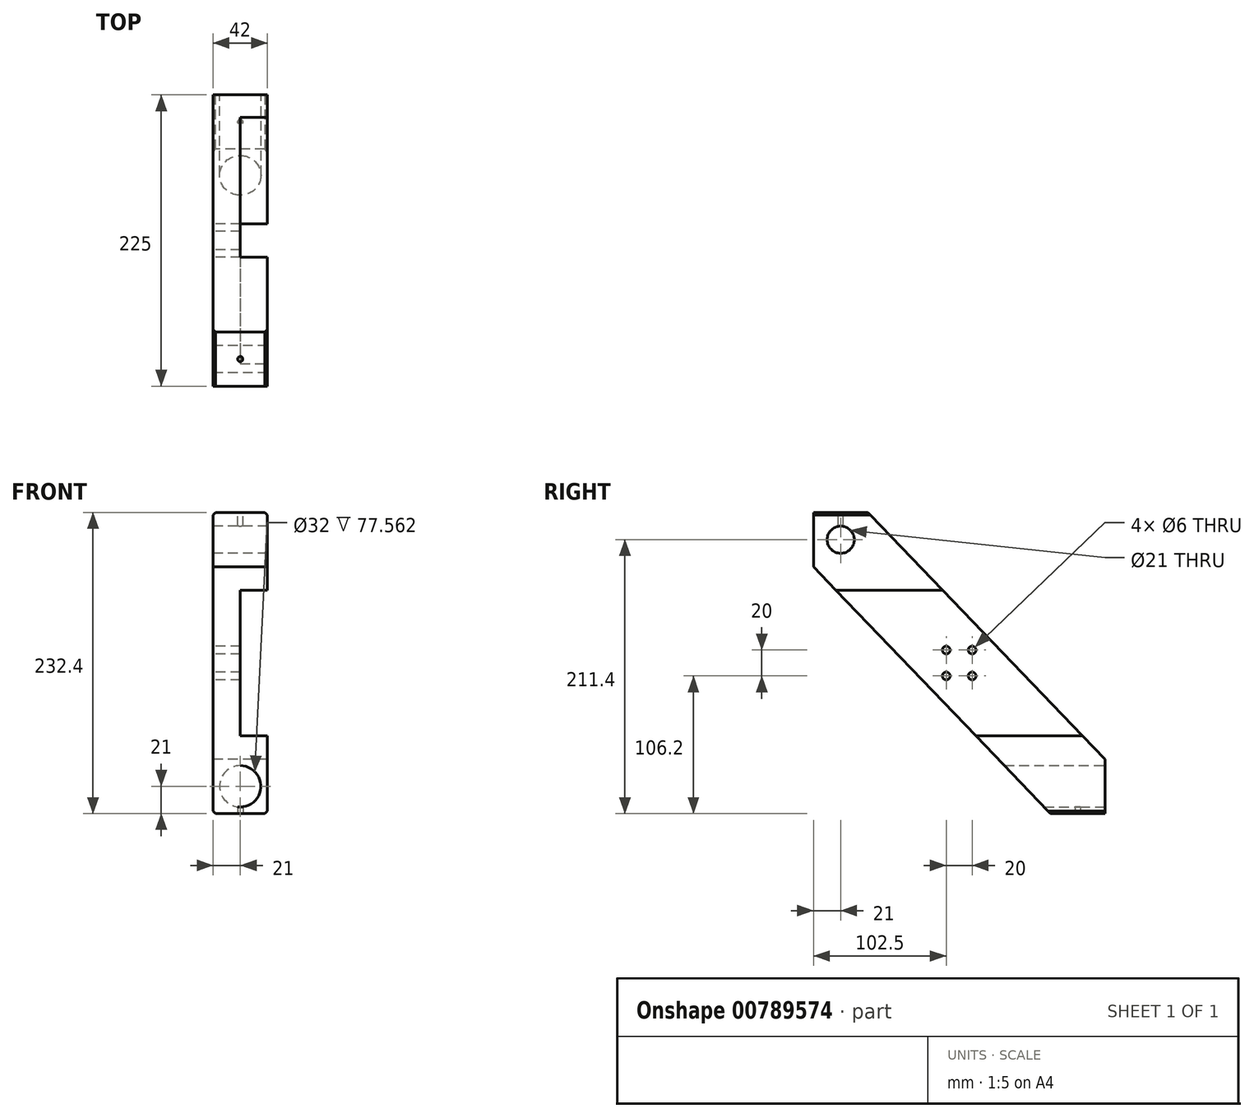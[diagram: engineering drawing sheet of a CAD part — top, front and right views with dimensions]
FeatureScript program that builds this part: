
annotation { "Feature Type Name" : "Feature", "Feature Type Description" : "" }
export const myFeature = defineFeature(function(context is Context, id is Id, definition is map)
    precondition{}
    {
        {
            var Q0;
            Q0=qCreatedBy(makeId("Right.planeOp"),FACE);
            var sketch = newSketch(context, id + "F0", { "sketchPlane" : qUnion([Q0])});
            skLineSegment(sketch, "E0.top", {"start": v(112.5, -116.2) * mm, "end": v(70.5, -116.2) * mm});
            skLineSegment(sketch, "E0.right", {"start": v(-112.5, 116.2) * mm, "end": v(-112.5, 74.2) * mm});
            skCircle(sketch, "E1", {"center": v(-91.5, 95.2) * mm, "radius": 10.5 * mm});
            skPoint(sketch, "E2", {"position": v(0, 0) * mm});
            skPoint(sketch, "E3.trimOffspring.end.orphan", {"position": v(-112.5, 116.2) * mm});
            skPoint(sketch, "E4", {"position": v(70.5, -116.2) * mm});
            skPoint(sketch, "E5", {"position": v(112.5, -74.2) * mm});
            skPoint(sketch, "E6", {"position": v(-112.5, 74.2) * mm});
            skLineSegment(sketch, "E7", {"start": v(70.5, -116.2) * mm, "end": v(-112.5, 74.2) * mm});
            skPoint(sketch, "E8", {"position": v(-70.5, 116.2) * mm});
            skLineSegment(sketch, "E9", {"start": v(112.5, -74.2) * mm, "end": v(-70.5, 116.2) * mm});
            skLineSegment(sketch, "E10.trimOffspring", {"start": v(-70.5, 116.2) * mm, "end": v(-112.5, 116.2) * mm});
            skLineSegment(sketch, "E11.trimOffspring", {"start": v(112.5, -74.2) * mm, "end": v(112.5, -116.2) * mm});
            skPoint(sketch, "E12", {"position": v(10, 10) * mm});
            skPoint(sketch, "E13", {"position": v(10, -10) * mm});
            skPoint(sketch, "E14", {"position": v(-10, -10) * mm});
            skPoint(sketch, "E15", {"position": v(-10, 10) * mm});
            skCircle(sketch, "E16", {"center": v(10, 10) * mm, "radius": 3 * mm});
            skCircle(sketch, "E17", {"center": v(-10, 10) * mm, "radius": 3 * mm});
            skCircle(sketch, "E18", {"center": v(10, -10) * mm, "radius": 3 * mm});
            skCircle(sketch, "E19", {"center": v(-10, -10) * mm, "radius": 3 * mm});
            skSolve(sketch);
        }
        {
            var Q0;
            Q0=makeQuery(id+"F0.imprint","IMPRINT",FACE,{"disambiguationData":[TD([[makeQuery(id+"F0.imprint","IMPRINT",EDGE,{"derivedFrom":sQuery(id+"F0.wireOp",EDGE,"E0.top")}),-1.0]])]});
            extrude(context, id + "F1", {"entities" : qUnion([Q0]), "depth" : 42 * mm, "offsetDistance" : 25 * mm});
        }
        {
            var Q0;
            Q0=makeQuery(id+"F1.opExtrude","CAP_FACE",FACE,{"disambiguationData":[OSD([sQuery(id+"F0.wireOp",EDGE,"E0.top"),sQuery(id+"F0.wireOp",EDGE,"E0.right"),sQuery(id+"F0.wireOp",EDGE,"E1"),sQuery(id+"F0.wireOp",EDGE,"E7"),sQuery(id+"F0.wireOp",EDGE,"E9"),sQuery(id+"F0.wireOp",EDGE,"E10.trimOffspring"),sQuery(id+"F0.wireOp",EDGE,"E11.trimOffspring"),sQuery(id+"F0.wireOp",EDGE,"E16"),sQuery(id+"F0.wireOp",EDGE,"E17"),sQuery(id+"F0.wireOp",EDGE,"E18"),sQuery(id+"F0.wireOp",EDGE,"E19")])],"isStart":false});
            var sketch = newSketch(context, id + "F2", { "sketchPlane" : qUnion([Q0])});
            skLineSegment(sketch, "E20", {"start": v(95.2, -56.2) * mm, "end": v(12.83, -56.2) * mm});
            skLineSegment(sketch, "E21", {"start": v(-12.83, 56.2) * mm, "end": v(-95.2, 56.2) * mm});
            skLineSegment(sketch, "E22", {"start": v(12.83, -56.2) * mm, "end": v(-95.2, 56.2) * mm});
            skLineSegment(sketch, "E23", {"start": v(-12.83, 56.2) * mm, "end": v(95.2, -56.2) * mm});
            skSolve(sketch);
        }
        {
            var Q0;
            Q0=makeQuery(id+"F2.imprint","IMPRINT",FACE,{"disambiguationData":[TD([[makeQuery(id+"F2.imprint","IMPRINT",EDGE,{"derivedFrom":sQuery(id+"F2.wireOp",EDGE,"E20")}),-1.0]])]});
            extrude(context, id + "F3", {"entities" : qUnion([Q0]), "operationType" : NewBodyOperationType.REMOVE, "oppositeDirection" : true, "depth" : 21 * mm, "offsetDistance" : 25 * mm});
        }
        {
            var Q0;
            Q0=makeQuery(id+"F1.opExtrude","SWEPT_FACE",FACE,{"disambiguationData":[OSD([sQuery(id+"F0.wireOp",EDGE,"E11.trimOffspring")])]});
            var sketch = newSketch(context, id + "F4", { "sketchPlane" : qUnion([Q0])});
            skPoint(sketch, "E24", {"position": v(-21, -95.2) * mm});
            skPoint(sketch, "E24.positionSnap0", {"position": v(-42, -95.2) * mm});
            skPoint(sketch, "E24.positionSnap1", {"position": v(-21, -116.2) * mm});
            skCircle(sketch, "E25", {"center": v(-21, -95.2) * mm, "radius": 16 * mm});
            skSolve(sketch);
        }
        {
            var Q0;
            Q0=makeQuery(id+"F4.imprint","IMPRINT",FACE,{"disambiguationData":[TD([[makeQuery(id+"F4.imprint","IMPRINT",EDGE,{"derivedFrom":sQuery(id+"F4.wireOp",EDGE,"E25")}),1.0]])]});
            extrude(context, id + "F5", {"entities" : qUnion([Q0]), "operationType" : NewBodyOperationType.REMOVE, "oppositeDirection" : true, "depth" : 85 * mm, "offsetDistance" : 25 * mm});
        }
        {
            var Q0;
            Q0=makeQuery(id+"F3.boolean.opBoolean","COPY",EDGE,{"derivedFrom":makeQuery(id+"F3.opExtrude","CAP_EDGE",EDGE,{"disambiguationData":[OSD([sQuery(id+"F2.wireOp",EDGE,"E23")])],"isStart":false})});
            var Q1;
            Q1=makeQuery(id+"F3.boolean.opBoolean","COPY",EDGE,{"derivedFrom":makeQuery(id+"F3.opExtrude","CAP_EDGE",EDGE,{"disambiguationData":[OSD([sQuery(id+"F2.wireOp",EDGE,"E22")])],"isStart":false})});
            var Q2;
            Q2=makeQuery(id+"F3.boolean.opBoolean","COPY",EDGE,{"derivedFrom":makeQuery(id+"F3.opExtrude","CAP_EDGE",EDGE,{"disambiguationData":[OSD([sQuery(id+"F2.wireOp",EDGE,"E21")])],"isStart":true})});
            var Q3;
            Q3=makeQuery(id+"F1.opExtrude","CAP_EDGE",EDGE,{"disambiguationData":[OSD([sQuery(id+"F0.wireOp",EDGE,"E10.trimOffspring")])],"isStart":true});
            var Q4;
            Q4=makeQuery(id+"F1.opExtrude","CAP_EDGE",EDGE,{"disambiguationData":[OSD([sQuery(id+"F0.wireOp",EDGE,"E0.top")])],"isStart":true});
            var Q5;
            Q5=makeQuery(id+"F3.boolean.opBoolean","COPY",EDGE,{"derivedFrom":makeQuery(id+"F3.opExtrude","CAP_EDGE",EDGE,{"disambiguationData":[OSD([sQuery(id+"F2.wireOp",EDGE,"E20")])],"isStart":true})});
            var Q6;
            Q6=makeQuery(id+"F1.opExtrude","CAP_EDGE",EDGE,{"disambiguationData":[OSD([sQuery(id+"F0.wireOp",EDGE,"E0.top")])],"isStart":false});
            var Q7;
            Q7=makeQuery(id+"F1.opExtrude","CAP_EDGE",EDGE,{"disambiguationData":[OSD([sQuery(id+"F0.wireOp",EDGE,"E10.trimOffspring")])],"isStart":false});
            chamfer(context, id + "F6", {"entities" : qUnion([Q0, Q1, Q2, Q3, Q4, Q5, Q6, Q7]), "width" : 2 * mm, "tangentPropagation" : true});
        }
        {
            var Q0;
            Q0=makeQuery(id+"F1.opExtrude","SWEPT_FACE",FACE,{"disambiguationData":[OSD([sQuery(id+"F0.wireOp",EDGE,"E10.trimOffspring")])]});
            var sketch = newSketch(context, id + "F7", { "sketchPlane" : qUnion([Q0])});
            skPoint(sketch, "E26", {"position": v(21, -91.5) * mm});
            skPoint(sketch, "E26.positionSnap0", {"position": v(2, -91.5) * mm});
            skPoint(sketch, "E26.positionSnap1", {"position": v(21, -70.5) * mm});
            skCircle(sketch, "E27", {"center": v(21, -91.5) * mm, "radius": 2 * mm});
            skSolve(sketch);
        }
        {
            var Q0;
            Q0=makeQuery(id+"F7.imprint","IMPRINT",FACE,{"disambiguationData":[TD([[makeQuery(id+"F7.imprint","IMPRINT",EDGE,{"derivedFrom":sQuery(id+"F7.wireOp",EDGE,"E27")}),1.0]])]});
            extrude(context, id + "F8", {"entities" : qUnion([Q0]), "operationType" : NewBodyOperationType.REMOVE, "oppositeDirection" : true, "depth" : 25 * mm, "offsetDistance" : 25 * mm});
        }
        {
            var Q0;
            Q0=makeQuery(id+"F1.opExtrude","SWEPT_FACE",FACE,{"disambiguationData":[OSD([sQuery(id+"F0.wireOp",EDGE,"E0.top")])]});
            var sketch = newSketch(context, id + "F9", { "sketchPlane" : qUnion([Q0])});
            skPoint(sketch, "E28", {"position": v(21, -91.5) * mm});
            skPoint(sketch, "E28.positionSnap0", {"position": v(21, -70.5) * mm});
            skPoint(sketch, "E28.positionSnap1", {"position": v(2, -91.5) * mm});
            skCircle(sketch, "E29", {"center": v(21, -91.5) * mm, "radius": 2 * mm});
            skSolve(sketch);
        }
        {
            var Q0;
            Q0=makeQuery(id+"F9.imprint","IMPRINT",FACE,{"disambiguationData":[TD([[makeQuery(id+"F9.imprint","IMPRINT",EDGE,{"derivedFrom":sQuery(id+"F9.wireOp",EDGE,"E29")}),1.0]])]});
            extrude(context, id + "F10", {"entities" : qUnion([Q0]), "operationType" : NewBodyOperationType.REMOVE, "oppositeDirection" : true, "depth" : 25 * mm, "offsetDistance" : 25 * mm});
        }
    });
